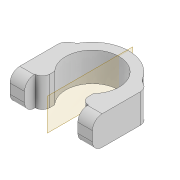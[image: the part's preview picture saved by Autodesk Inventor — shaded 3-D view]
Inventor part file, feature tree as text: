
AUTODESK INVENTOR PART (.ipt)
format: ipt  version: 2022 (Build 260153000, 153)  size: 166,400 bytes
history: native  units: mm
features: fillet x3, extrude x2, sketch x2, projected_geometry x2, mirror x1
ambient origin geometry x8: Origin, YZ Plane, XZ Plane, XY Plane, X Axis, Y Axis, Z Axis, Center Point
bodies: Solid1 (feature_tree)
feature tree (10):
  extrude  "Extrusion1"  Depth=2.0mm
  fillet  "Fillet1"  Radius=1.0mm
  extrude  "Extrusion3"  Depth=1.5mm
  fillet  "Fillet2"  Radius=6.0mm
  mirror  "Mirror1"
  fillet  "Fillet5"  Radius=1.5mm
  sketch  "Sketch1"  dims[d0=11.0mm d1=2.0mm d3=1.0mm]
  sketch  "Sketch4"  dims[d4=1.5mm d5=1.5mm d6=6.0mm d7=0.0mm d8=1.5mm d14=2.0mm d15=0.0mm d16=2.0mm d22=3.0mm d29=2.0mm d28=0.5mm d30=0.5mm d31=0.872665mm d32=0.0mm]
  projected_geometry  "Projected Loop2"
  projected_geometry  "Projected Loop4"
